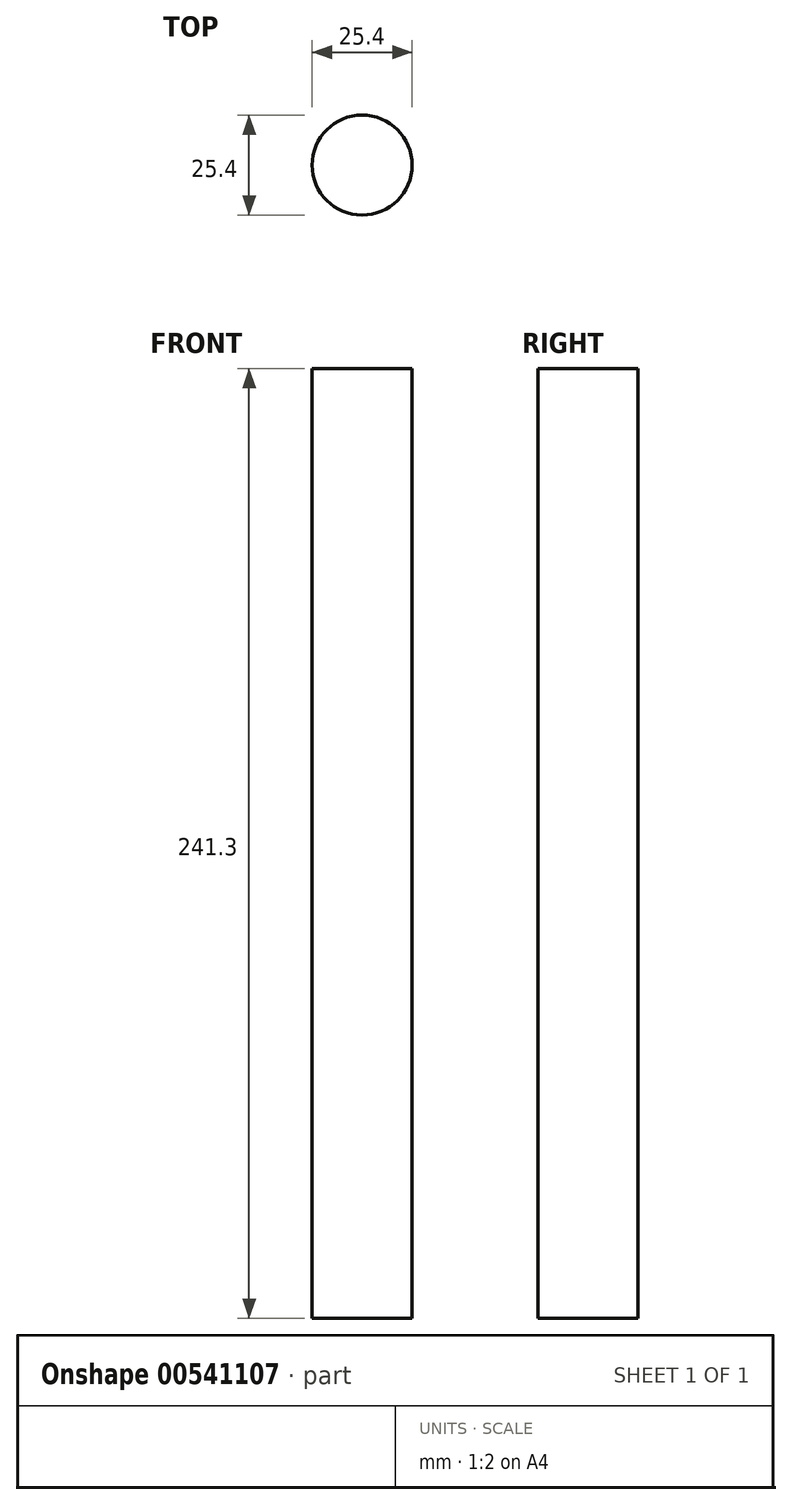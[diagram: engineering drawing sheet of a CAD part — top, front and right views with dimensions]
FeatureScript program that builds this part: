
annotation { "Feature Type Name" : "Feature", "Feature Type Description" : "" }
export const myFeature = defineFeature(function(context is Context, id is Id, definition is map)
    precondition{}
    {
        {
            var Q0;
            Q0=qCreatedBy(makeId("Top.planeOp"),FACE);
            var sketch = newSketch(context, id + "F0", { "sketchPlane" : qUnion([Q0])});
            skCircle(sketch, "E0", {"center": v(0, 0) * mm, "radius": 12.7 * mm});
            skSolve(sketch);
        }
        {
            var Q0;
            Q0=makeQuery(id+"F0.imprint","IMPRINT",FACE,{"disambiguationData":[TD([[makeQuery(id+"F0.imprint","IMPRINT",EDGE,{"derivedFrom":sQuery(id+"F0.wireOp",EDGE,"E0")}),1.0]])]});
            extrude(context, id + "F1", {"entities" : qUnion([Q0]), "depth" : 241.3 * mm, "offsetDistance" : 25.4 * mm});
        }
    });
